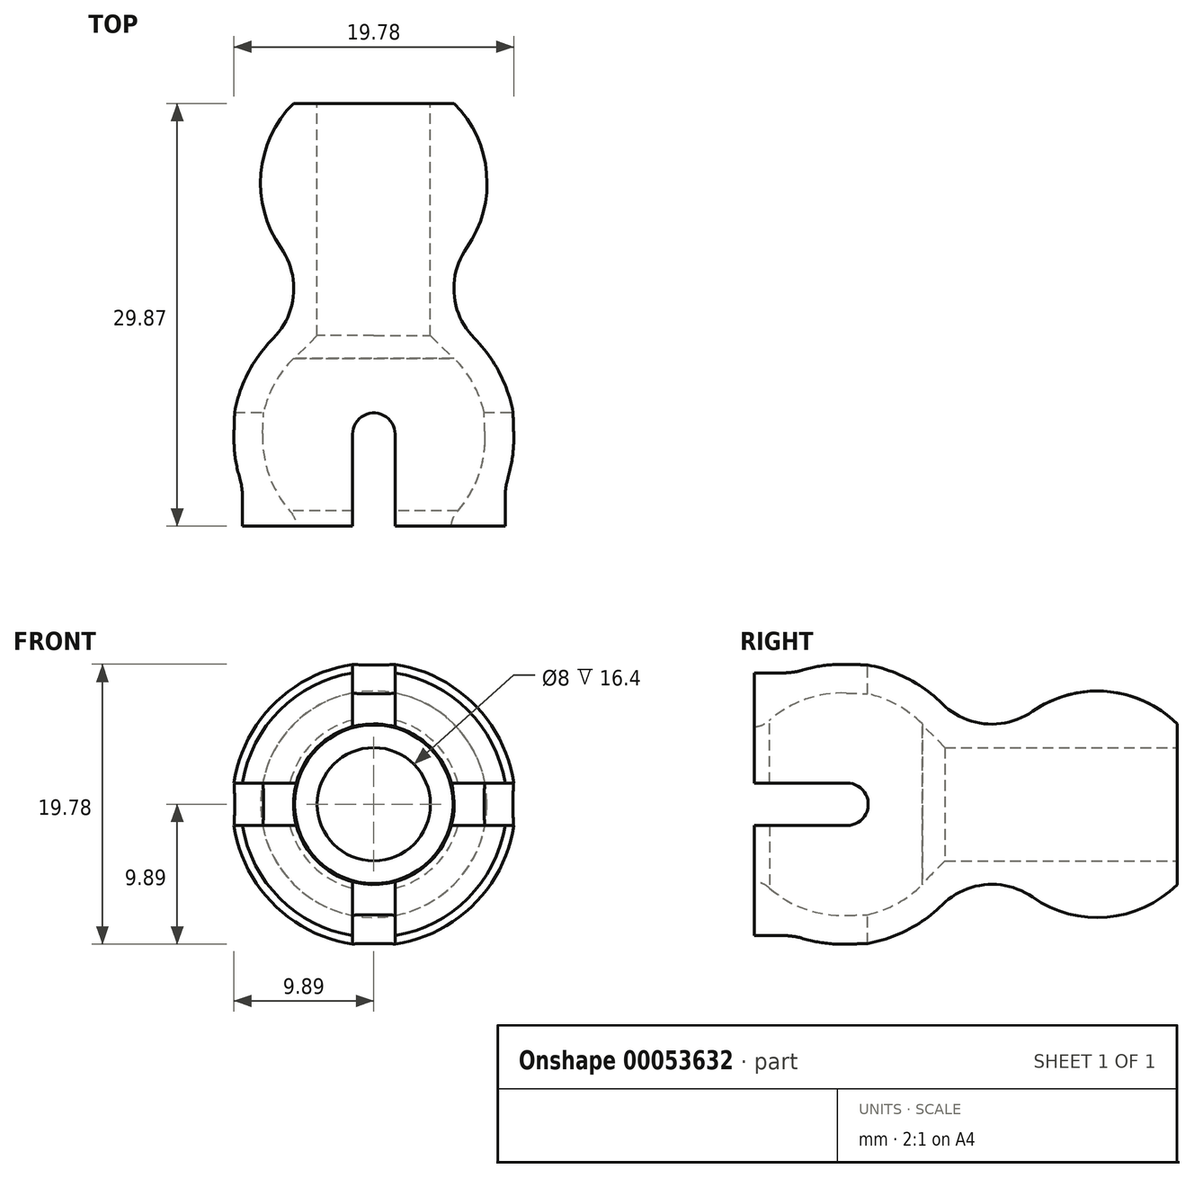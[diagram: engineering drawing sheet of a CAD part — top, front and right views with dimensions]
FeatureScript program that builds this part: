
annotation { "Feature Type Name" : "Feature", "Feature Type Description" : "" }
export const myFeature = defineFeature(function(context is Context, id is Id, definition is map)
    precondition{}
    {
        {
            var Q0;
            Q0=qCreatedBy(makeId("Top.planeOp"),FACE);
            var sketch = newSketch(context, id + "F0", { "sketchPlane" : qUnion([Q0])});
            skArc(sketch, "E0", {"start": v(6.56, -4.58) * mm, "mid": v(7.97, 0.69) * mm, "end": v(5.68, 5.64) * mm});
            skPoint(sketch, "E1.visualSharp", {"position": v(0, -8) * mm});
            skArc(sketch, "E1.filletArc", {"start": v(6.56, -4.58) * mm, "mid": v(5.68, -7.87) * mm, "end": v(7.1, -10.96) * mm});
            skPoint(sketch, "E2.orphan", {"position": v(0, -28) * mm});
            skArc(sketch, "E3", {"start": v(6.03, -23.25) * mm, "mid": v(8, -17.74) * mm, "end": v(5.68, -12.36) * mm});
            skLineSegment(sketch, "E4", {"start": v(0, 5.64) * mm, "end": v(0, -10) * mm});
            skArc(sketch, "E5", {"start": v(6.13, -23.14) * mm, "mid": v(5.8, -23.64) * mm, "end": v(5.68, -24.23) * mm});
            skPoint(sketch, "E6.start.orphan", {"position": v(5.68, -7.87) * mm});
            skLineSegment(sketch, "E7", {"start": v(5.68, -12.36) * mm, "end": v(0, -12.36) * mm});
            skLineSegment(sketch, "E8", {"start": v(0, -12.36) * mm, "end": v(0, -10) * mm});
            skLineSegment(sketch, "E9", {"start": v(0, 5.64) * mm, "end": v(5.68, 5.64) * mm});
            skLineSegment(sketch, "E10", {"start": v(0, -12.36) * mm, "end": v(0, -28) * mm, "construction": true});
            skLineSegment(sketch, "E11", {"start": v(5.68, -24.23) * mm, "end": v(7.83, -24.23) * mm});
            skLineSegment(sketch, "E12", {"start": v(9.4, -22.2) * mm, "end": v(9.4, -24.23) * mm});
            skLineSegment(sketch, "E13", {"start": v(7.83, -24.23) * mm, "end": v(9.4, -24.23) * mm});
            skArc(sketch, "E14.trimOffspring", {"start": v(9.6, -20.8) * mm, "mid": v(9.7, -15.54) * mm, "end": v(7.1, -10.96) * mm});
            skPoint(sketch, "E15.visualSharp", {"position": v(9.4, -21.4) * mm});
            skArc(sketch, "E15.filletArc", {"start": v(9.6, -20.8) * mm, "mid": v(9.45, -21.5) * mm, "end": v(9.4, -22.2) * mm});
            skSolve(sketch);
        }
        {
            var Q0;
            Q0 = qSketchRegion(id + "F0", true);
            var Q1;
            Q1=sQuery(id+"F0.wireOp",EDGE,"E10");
            revolve(context, id + "F1", {"entities" : qUnion([Q0]), "axis" : qUnion([Q1]), "revolveType" : RevolveType.FULL});
        }
        {
            var Q0;
            Q0=qCreatedBy(makeId("Top.planeOp"),FACE);
            var sketch = newSketch(context, id + "F2", { "sketchPlane" : qUnion([Q0])});
            skLineSegment(sketch, "E16.bottom", {"start": v(-1.5, -24.23) * mm, "end": v(1.5, -24.23) * mm});
            skLineSegment(sketch, "E16.left", {"start": v(-1.5, -24.23) * mm, "end": v(-1.5, -17.73) * mm});
            skLineSegment(sketch, "E16.right", {"start": v(1.5, -24.23) * mm, "end": v(1.5, -17.73) * mm});
            skArc(sketch, "E17", {"start": v(1.5, -17.73) * mm, "mid": v(0, -16.23) * mm, "end": v(-1.5, -17.73) * mm});
            skSolve(sketch);
        }
        {
            var Q0;
            Q0 = qSketchRegion(id + "F2", true);
            extrude(context, id + "F3", {"entities" : qUnion([Q0]), "operationType" : NewBodyOperationType.REMOVE, "endBound" : BoundingType.SYMMETRIC, "oppositeDirection" : true, "depth" : 25 * mm});
        }
        {
            var Q0;
            Q0=qCreatedBy(makeId("Right.planeOp"),FACE);
            var sketch = newSketch(context, id + "F4", { "sketchPlane" : qUnion([Q0])});
            skLineSegment(sketch, "E18.bottom", {"start": v(-25.68, 1.5) * mm, "end": v(-17.68, 1.5) * mm});
            skLineSegment(sketch, "E18.top", {"start": v(-25.68, -1.5) * mm, "end": v(-17.68, -1.5) * mm});
            skLineSegment(sketch, "E18.left", {"start": v(-25.68, 1.5) * mm, "end": v(-25.68, -1.5) * mm});
            skArc(sketch, "E19", {"start": v(-17.68, -1.5) * mm, "mid": v(-16.18, 0) * mm, "end": v(-17.68, 1.5) * mm});
            skSolve(sketch);
        }
        {
            var Q0;
            Q0 = qSketchRegion(id + "F4", true);
            extrude(context, id + "F5", {"entities" : qUnion([Q0]), "operationType" : NewBodyOperationType.REMOVE, "endBound" : BoundingType.SYMMETRIC, "oppositeDirection" : true, "depth" : 25 * mm});
        }
        {
            var Q0;
            Q0=makeQuery(id+"F1.opRevolve","SWEPT_FACE",FACE,{"disambiguationData":[OSD([sQuery(id+"F0.wireOp",EDGE,"E9")])]});
            var sketch = newSketch(context, id + "F6", { "sketchPlane" : qUnion([Q0])});
            skCircle(sketch, "E20", {"center": v(0, 0) * mm, "radius": 4 * mm});
            skSolve(sketch);
        }
        {
            var Q0;
            Q0 = qSketchRegion(id + "F6", true);
            extrude(context, id + "F7", {"entities" : qUnion([Q0]), "operationType" : NewBodyOperationType.REMOVE, "endBound" : BoundingType.THROUGH_ALL, "oppositeDirection" : true, "depth" : 25 * mm});
        }
        {
            var Q0;
            Q0=makeQuery(id+"F7.boolean.opBoolean","INTERSECT",EDGE,{"derivedFrom":[makeQuery(id+"F1.opRevolve","SWEPT_FACE",FACE,{"disambiguationData":[OSD([sQuery(id+"F0.wireOp",EDGE,"E7")])]}),makeQuery(id+"F7.opExtrude","SWEPT_FACE",FACE,{"disambiguationData":[OSD([sQuery(id+"F6.wireOp",EDGE,"E20")])]})]});
            chamfer(context, id + "F8", {"entities" : qUnion([Q0]), "width" : 1.6 * mm, "tangentPropagation" : true});
        }
    });
